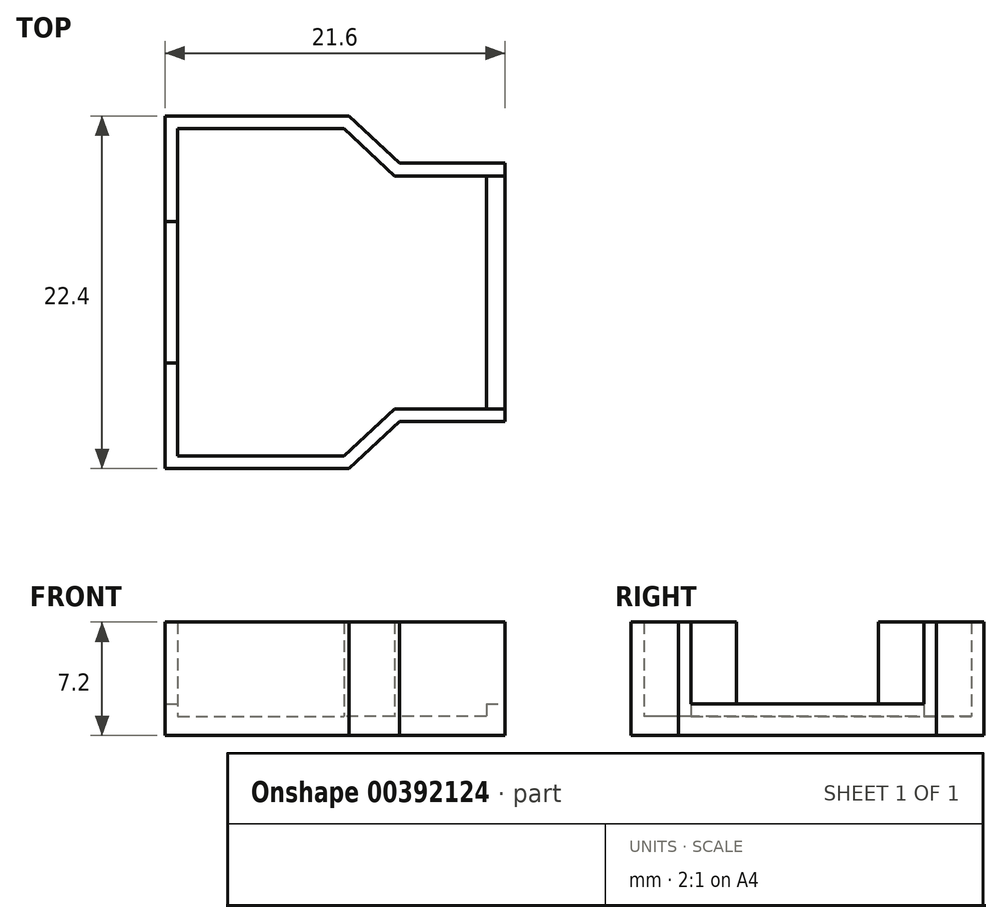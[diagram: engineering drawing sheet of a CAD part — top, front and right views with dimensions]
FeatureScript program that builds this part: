
annotation { "Feature Type Name" : "Feature", "Feature Type Description" : "" }
export const myFeature = defineFeature(function(context is Context, id is Id, definition is map)
    precondition{}
    {
        {
            var Q0;
            Q0=qCreatedBy(makeId("Top.planeOp"),FACE);
            var sketch = newSketch(context, id + "F0", { "sketchPlane" : qUnion([Q0])});
            skLineSegment(sketch, "E0.0", {"start": v(8.67, 8.2) * mm, "end": v(15.4, 8.2) * mm});
            skLineSegment(sketch, "E0.1", {"start": v(5.47, 11.2) * mm, "end": v(8.67, 8.2) * mm});
            skLineSegment(sketch, "E0.2", {"start": v(15.4, 8.2) * mm, "end": v(15.4, -8.2) * mm});
            skLineSegment(sketch, "E0.3", {"start": v(5.47, 11.2) * mm, "end": v(-6.2, 11.2) * mm});
            skLineSegment(sketch, "E0.4", {"start": v(-6.2, -11.2) * mm, "end": v(-6.2, 11.2) * mm});
            skLineSegment(sketch, "E0.7", {"start": v(5.47, -11.2) * mm, "end": v(8.67, -8.2) * mm});
            skLineSegment(sketch, "E0.8", {"start": v(5.47, -11.2) * mm, "end": v(-6.2, -11.2) * mm});
            skLineSegment(sketch, "E1.bottom", {"start": v(-6.2, 4.5) * mm, "end": v(-5.4, 4.5) * mm});
            skLineSegment(sketch, "E1.top", {"start": v(-6.2, -4.5) * mm, "end": v(-5.4, -4.5) * mm});
            skLineSegment(sketch, "E1.left", {"start": v(-6.2, 4.5) * mm, "end": v(-6.2, -4.5) * mm});
            skLineSegment(sketch, "E2.0", {"start": v(8.36, 7.4) * mm, "end": v(14.2, 7.4) * mm});
            skLineSegment(sketch, "E2.1", {"start": v(5.16, 10.4) * mm, "end": v(8.36, 7.4) * mm});
            skLineSegment(sketch, "E2.2", {"start": v(5.16, 10.4) * mm, "end": v(-5.4, 10.4) * mm});
            skLineSegment(sketch, "E2.3", {"start": v(-5.4, -10.4) * mm, "end": v(-5.4, 10.4) * mm});
            skLineSegment(sketch, "E2.6", {"start": v(5.16, -10.4) * mm, "end": v(8.36, -7.4) * mm});
            skLineSegment(sketch, "E2.7", {"start": v(5.16, -10.4) * mm, "end": v(-5.4, -10.4) * mm});
            skLineSegment(sketch, "E3", {"start": v(14.2, 7.4) * mm, "end": v(14.2, -7.4) * mm});
            skLineSegment(sketch, "E4", {"start": v(14.2, 7.4) * mm, "end": v(15.4, 7.4) * mm});
            skLineSegment(sketch, "E5", {"start": v(14.2, -7.4) * mm, "end": v(15.4, -7.4) * mm});
            skLineSegment(sketch, "E6", {"start": v(8.36, -7.4) * mm, "end": v(14.2, -7.4) * mm});
            skLineSegment(sketch, "E7", {"start": v(8.67, -8.2) * mm, "end": v(15.4, -8.2) * mm});
            skSolve(sketch);
        }
        {
            var Q0;
            Q0=makeQuery(id+"F0.imprint","IMPRINT",FACE,{"disambiguationData":[TD([[makeQuery(id+"F0.imprint","IMPRINT",EDGE,{"derivedFrom":sQuery(id+"F0.wireOp",EDGE,"E2.0")}),-1.0]])]});
            var Q1;
            {var subQ5=sQuery(id+"F0.wireOp",EDGE,"E0.0");Q1=makeQuery(id+"F0.imprint","IMPRINT",FACE,{"disambiguationData":[TD([[makeQuery(id+"F0.imprint","IMPRINT",EDGE,{"derivedFrom":subQ5}),-1.0]])]});}
            var Q2;
            {var subQ0=sQuery(id+"F0.wireOp",EDGE,"E1.bottom");Q2=makeQuery(id+"F0.imprint","IMPRINT",FACE,{"disambiguationData":[TD([[makeQuery(id+"F0.imprint","IMPRINT",EDGE,{"derivedFrom":subQ0}),-1.0]])]});}
            var Q3;
            Q3=makeQuery(id+"F0.imprint","IMPRINT",FACE,{"disambiguationData":[TD([[makeQuery(id+"F0.imprint","IMPRINT",EDGE,{"derivedFrom":sQuery(id+"F0.wireOp",EDGE,"E0.7")}),1.0]])]});
            var Q4;
            Q4=makeQuery(id+"F0.imprint","IMPRINT",FACE,{"disambiguationData":[TD([[makeQuery(id+"F0.imprint","IMPRINT",EDGE,{"derivedFrom":sQuery(id+"F0.wireOp",EDGE,"E3")}),1.0]])]});
            extrude(context, id + "F1", {"entities" : qUnion([Q0, Q1, Q2, Q3, Q4]), "depth" : 1.2 * mm});
        }
        {
            var Q0;
            {var subQ0=sQuery(id+"F0.wireOp",EDGE,"E1.bottom");Q0=makeQuery(id+"F0.imprint","IMPRINT",FACE,{"disambiguationData":[TD([[makeQuery(id+"F0.imprint","IMPRINT",EDGE,{"derivedFrom":subQ0}),-1.0]])]});}
            extrude(context, id + "F2", {"entities" : qUnion([Q0]), "operationType" : NewBodyOperationType.ADD, "depth" : 2 * mm});
        }
        {
            var Q0;
            Q0=makeQuery(id+"F0.imprint","IMPRINT",FACE,{"disambiguationData":[TD([[makeQuery(id+"F0.imprint","IMPRINT",EDGE,{"derivedFrom":sQuery(id+"F0.wireOp",EDGE,"E3")}),1.0]])]});
            extrude(context, id + "F3", {"entities" : qUnion([Q0]), "operationType" : NewBodyOperationType.ADD, "depth" : 2 * mm});
        }
        {
            var Q0;
            {var subQ5=sQuery(id+"F0.wireOp",EDGE,"E0.0");Q0=makeQuery(id+"F0.imprint","IMPRINT",FACE,{"disambiguationData":[TD([[makeQuery(id+"F0.imprint","IMPRINT",EDGE,{"derivedFrom":subQ5}),-1.0]])]});}
            var Q1;
            Q1=makeQuery(id+"F0.imprint","IMPRINT",FACE,{"disambiguationData":[TD([[makeQuery(id+"F0.imprint","IMPRINT",EDGE,{"derivedFrom":sQuery(id+"F0.wireOp",EDGE,"E0.7")}),1.0]])]});
            extrude(context, id + "F4", {"entities" : qUnion([Q0, Q1]), "operationType" : NewBodyOperationType.ADD, "depth" : 7.2 * mm});
        }
    });
